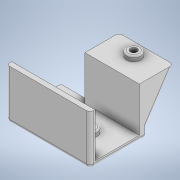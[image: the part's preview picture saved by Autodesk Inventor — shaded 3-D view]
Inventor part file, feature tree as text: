
AUTODESK INVENTOR PART (.ipt)
format: ipt  version: 2020 (Build 240168000, 168)  size: 266,240 bytes
history: native  units: in
note: dims shown in document units (in); Inventor stores cm internally (conversion verified against a paired STEP export)
features: extrude x14, sketch x14, fillet x2
ambient origin geometry x8: Origin, YZ Plane, XZ Plane, XY Plane, X Axis, Y Axis, Z Axis, Center Point
bodies: Solid1 (feature_tree)
feature tree (30):
  extrude  "Extrusion1"  Depth=1.2756in
  extrude  "Extrusion4"  Depth=0.1181in
  extrude  "Extrusion5"  Depth=0.1181in
  extrude  "Extrusion6"  Depth=0.1181in
  extrude  "Extrusion7"  Depth=0.1181in TaperAngle=0.0deg
  extrude  "Extrusion8"  Depth=0.1575in
  extrude  "Extrusion15"  Depth=0.2362in
  extrude  "Extrusion23"  Depth=0.1181in TaperAngle=0.0deg
  extrude  "Extrusion24"  Depth=1.2756in
  extrude  "Extrusion25"  Depth=1.0394in TaperAngle=0.0deg
  extrude  "Extrusion26"  Depth=0.1181in
  extrude  "Extrusion27"  Depth=0.6811in TaperAngle=0.0deg
  extrude  "Extrusion28"  Depth=1.2756in
  fillet  "Fillet3"  Radius=1.2756in
  fillet  "Fillet4"  Radius=0.3346in
  extrude  "Extrusion29"  Depth=0.1181in
  sketch  "Sketch1"  dims[d0=1.6142in d1=1.2756in]
  sketch  "Sketch4"  dims[d2=0.1181in d3=0.0in d12=0.8465in]
  sketch  "Sketch5"  dims[d13=0.1181in d14=0.0in d15=0.8465in]
  sketch  "Sketch6"  dims[d16=0.1181in d17=0.0in d20=0.3346in]
  sketch  "Sketch7"  dims[d21=0.3346in d22=0.1181in d23=0.0in]
  sketch  "Sketch8"  dims[d24=0.1575in d25=0.1575in]
  sketch  "Sketch15"  dims[d26=0.2362in d27=0.0in d28=0.2362in]
  sketch  "Sketch23"  dims[d29=0.2362in d30=0.1181in d31=0.0in]
  sketch  "Sketch24"  dims[d54=0.3425in d55=0.0in d81=1.2756in]
  sketch  "Sketch25"  dims[d82=0.1181in d83=1.0394in d84=0.0in]
  sketch  "Sketch26"  dims[d85=0.1181in d86=0.1181in]
  sketch  "Sketch27"  dims[d87=0.1181in d88=0.6811in d89=0.0in]
  sketch  "Sketch28"  dims[d90=1.2756in d91=0.0in d92=0.1575in d93=1.2756in d94=0.0in d95=0.3346in]
  sketch  "Sketch29"  dims[d96=0.1181in d97=0.0in d98=0.1181in d99=1.0394in d100=0.0in d101=0.0394in d102=0.0787in d103=0.2362in d104=0.1181in d105=0.0in d10=0.0197in d11=0.0344in d65=0.0197in d66=0.0344in d67=0.0197in d68=0.0344in]
